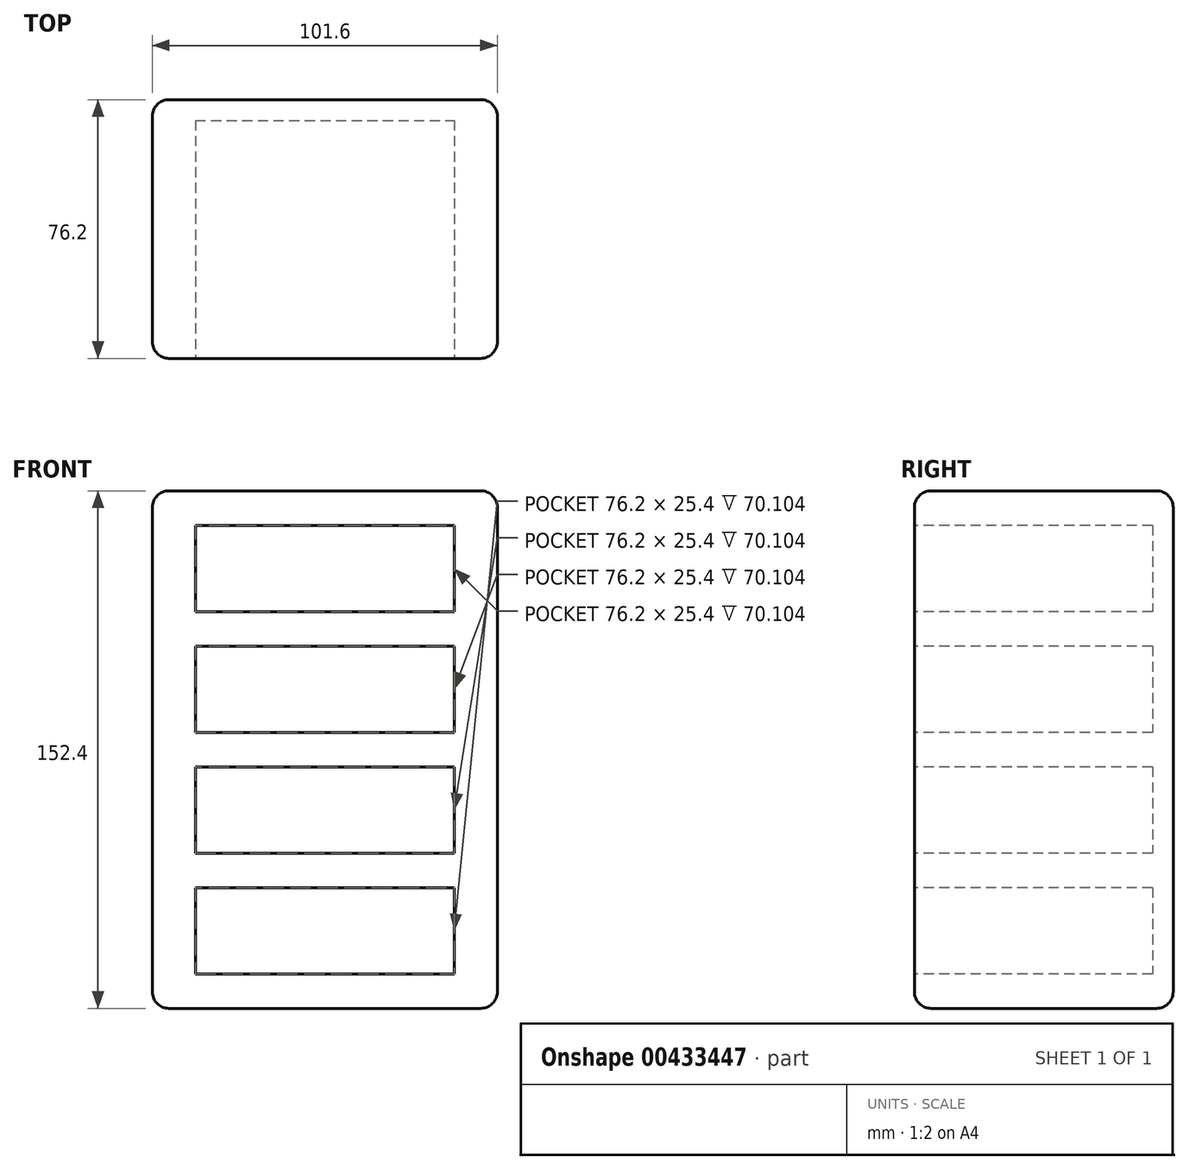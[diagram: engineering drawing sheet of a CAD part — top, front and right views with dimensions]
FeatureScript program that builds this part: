
annotation { "Feature Type Name" : "Feature", "Feature Type Description" : "" }
export const myFeature = defineFeature(function(context is Context, id is Id, definition is map)
    precondition{}
    {
        {
            var Q0;
            Q0=qCreatedBy(makeId("Top.planeOp"),FACE);
            var sketch = newSketch(context, id + "F0", { "sketchPlane" : qUnion([Q0])});
            skLineSegment(sketch, "E0.bottom", {"start": v(-12.28, -34.28) * mm, "end": v(89.32, -34.28) * mm});
            skLineSegment(sketch, "E0.top", {"start": v(-12.28, -110.48) * mm, "end": v(89.32, -110.48) * mm});
            skLineSegment(sketch, "E0.left", {"start": v(-12.28, -34.28) * mm, "end": v(-12.28, -110.48) * mm});
            skLineSegment(sketch, "E0.right", {"start": v(89.32, -34.28) * mm, "end": v(89.32, -110.48) * mm});
            skSolve(sketch);
        }
        {
            var Q0;
            Q0=makeQuery(id+"F0.imprint","IMPRINT",FACE,{"disambiguationData":[TD([[makeQuery(id+"F0.imprint","IMPRINT",EDGE,{"derivedFrom":sQuery(id+"F0.wireOp",EDGE,"E0.bottom")}),-1.0]])]});
            extrude(context, id + "F1", {"entities" : qUnion([Q0]), "depth" : 152.4 * mm});
        }
        {
            var Q0;
            Q0=makeQuery(id+"F1.opExtrude","SWEPT_FACE",FACE,{"disambiguationData":[OSD([sQuery(id+"F0.wireOp",EDGE,"E0.top")])]});
            var sketch = newSketch(context, id + "F2", { "sketchPlane" : qUnion([Q0])});
            skLineSegment(sketch, "E1.bottom", {"start": v(0, 142.24) * mm, "end": v(76.62, 142.24) * mm});
            skLineSegment(sketch, "E1.top", {"start": v(0.42, 116.84) * mm, "end": v(76.62, 116.84) * mm});
            skLineSegment(sketch, "E1.left", {"start": v(0.42, 142.24) * mm, "end": v(0.42, 116.84) * mm});
            skLineSegment(sketch, "E1.right", {"start": v(76.62, 142.24) * mm, "end": v(76.62, 116.84) * mm});
            skLineSegment(sketch, "E2.0.1.0", {"start": v(0.42, 106.68) * mm, "end": v(0.42, 81.28) * mm});
            skLineSegment(sketch, "E2.0.1.1", {"start": v(0, 106.68) * mm, "end": v(76.62, 106.68) * mm});
            skLineSegment(sketch, "E2.0.1.2", {"start": v(0.42, 81.28) * mm, "end": v(76.62, 81.28) * mm});
            skLineSegment(sketch, "E2.0.1.3", {"start": v(76.62, 106.68) * mm, "end": v(76.62, 81.28) * mm});
            skLineSegment(sketch, "E2.0.2.0", {"start": v(0.42, 71.12) * mm, "end": v(0.42, 45.72) * mm});
            skLineSegment(sketch, "E2.0.2.1", {"start": v(0, 71.12) * mm, "end": v(76.62, 71.12) * mm});
            skLineSegment(sketch, "E2.0.2.2", {"start": v(0.42, 45.72) * mm, "end": v(76.62, 45.72) * mm});
            skLineSegment(sketch, "E2.0.2.3", {"start": v(76.62, 71.12) * mm, "end": v(76.62, 45.72) * mm});
            skLineSegment(sketch, "E2.0.3.0", {"start": v(0.42, 35.56) * mm, "end": v(0.42, 10.16) * mm});
            skLineSegment(sketch, "E2.0.3.1", {"start": v(0, 35.56) * mm, "end": v(76.62, 35.56) * mm});
            skLineSegment(sketch, "E2.0.3.2", {"start": v(0.42, 10.16) * mm, "end": v(76.62, 10.16) * mm});
            skLineSegment(sketch, "E2.0.3.3", {"start": v(76.62, 35.56) * mm, "end": v(76.62, 10.16) * mm});
            skLineSegment(sketch, "E2.direction1", {"start": v(0.42, 116.84) * mm, "end": v(25.82, 116.84) * mm, "construction": true});
            skLineSegment(sketch, "E2.direction2", {"start": v(0.42, 116.84) * mm, "end": v(0.42, 81.28) * mm, "construction": true});
            skSolve(sketch);
        }
        {
            var Q0;
            Q0=makeQuery(id+"F2.imprint","IMPRINT",FACE,{"disambiguationData":[TD([[makeQuery(id+"F2.imprint","IMPRINT",EDGE,{"derivedFrom":sQuery(id+"F2.wireOp",EDGE,"E1.top")}),1.0]])]});
            var Q1;
            {var subQ0=sQuery(id+"F2.wireOp",EDGE,"E2.0.1.0");Q1=makeQuery(id+"F2.imprint","IMPRINT",FACE,{"disambiguationData":[TD([[makeQuery(id+"F2.imprint","IMPRINT",EDGE,{"derivedFrom":subQ0}),1.0]])]});}
            var Q2;
            {var subQ0=sQuery(id+"F2.wireOp",EDGE,"E2.0.2.0");Q2=makeQuery(id+"F2.imprint","IMPRINT",FACE,{"disambiguationData":[TD([[makeQuery(id+"F2.imprint","IMPRINT",EDGE,{"derivedFrom":subQ0}),1.0]])]});}
            var Q3;
            {var subQ0=sQuery(id+"F2.wireOp",EDGE,"E2.0.3.0");Q3=makeQuery(id+"F2.imprint","IMPRINT",FACE,{"disambiguationData":[TD([[makeQuery(id+"F2.imprint","IMPRINT",EDGE,{"derivedFrom":subQ0}),1.0]])]});}
            extrude(context, id + "F3", {"entities" : qUnion([Q0, Q1, Q2, Q3]), "operationType" : NewBodyOperationType.REMOVE, "oppositeDirection" : true, "depth" : 70.1 * mm});
        }
        {
            var Q0;
            Q0=makeQuery(id+"F1.opExtrude","CAP_FACE",FACE,{"disambiguationData":[OSD([sQuery(id+"F0.wireOp",EDGE,"E0.bottom"),sQuery(id+"F0.wireOp",EDGE,"E0.top"),sQuery(id+"F0.wireOp",EDGE,"E0.left"),sQuery(id+"F0.wireOp",EDGE,"E0.right")])],"isStart":false});
            var Q1;
            Q1=makeQuery(id+"F1.opExtrude","SWEPT_FACE",FACE,{"disambiguationData":[OSD([sQuery(id+"F0.wireOp",EDGE,"E0.right")])]});
            var Q2;
            Q2=makeQuery(id+"F1.opExtrude","CAP_EDGE",EDGE,{"disambiguationData":[OSD([sQuery(id+"F0.wireOp",EDGE,"E0.top")])],"isStart":true});
            var Q3;
            Q3=makeQuery(id+"F1.opExtrude","SWEPT_EDGE",EDGE,{"disambiguationData":[OSD([sQuery(id+"F0.wireOp",EDGE,"E0.bottom"),sQuery(id+"F0.wireOp",EDGE,"E0.right")])]});
            var Q4;
            Q4=makeQuery(id+"F1.opExtrude","CAP_EDGE",EDGE,{"disambiguationData":[OSD([sQuery(id+"F0.wireOp",EDGE,"E0.bottom")])],"isStart":true});
            var Q5;
            Q5=makeQuery(id+"F1.opExtrude","SWEPT_EDGE",EDGE,{"disambiguationData":[OSD([sQuery(id+"F0.wireOp",EDGE,"E0.bottom"),sQuery(id+"F0.wireOp",EDGE,"E0.left")])]});
            var Q6;
            Q6=makeQuery(id+"F1.opExtrude","SWEPT_EDGE",EDGE,{"disambiguationData":[OSD([sQuery(id+"F0.wireOp",EDGE,"E0.top"),sQuery(id+"F0.wireOp",EDGE,"E0.left")])]});
            var Q7;
            Q7=makeQuery(id+"F1.opExtrude","CAP_EDGE",EDGE,{"disambiguationData":[OSD([sQuery(id+"F0.wireOp",EDGE,"E0.left")])],"isStart":true});
            fillet(context, id + "F4", {"entities" : qUnion([Q0, Q1, Q2, Q3, Q4, Q5, Q6, Q7]), "radius" : 4.9 * mm, "tangentPropagation" : true, "allowEdgeOverflow" : false});
        }
    });
